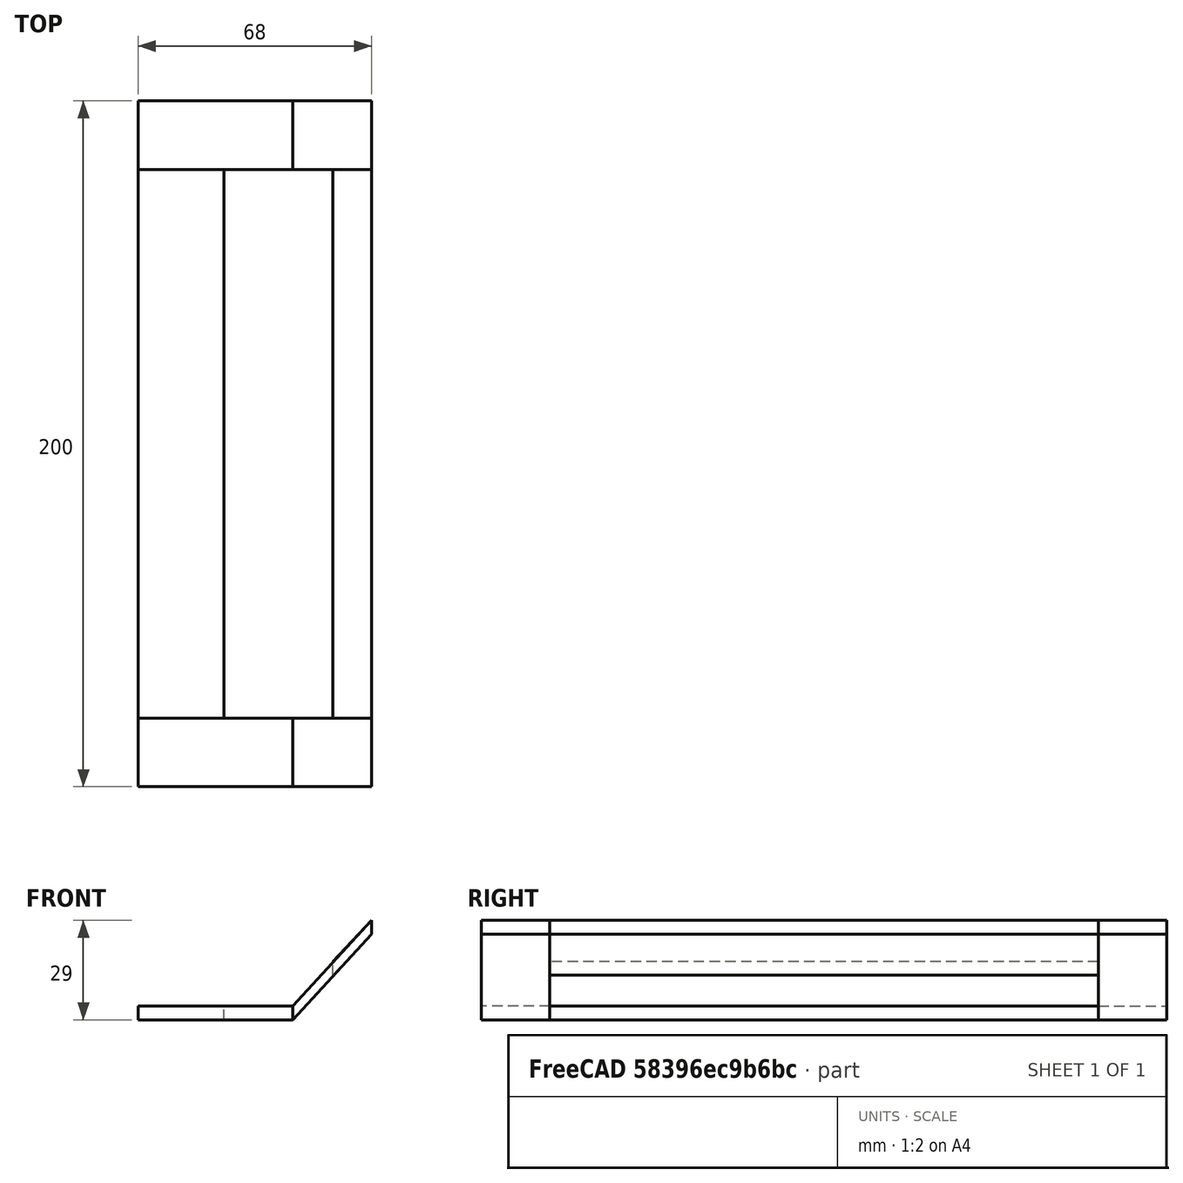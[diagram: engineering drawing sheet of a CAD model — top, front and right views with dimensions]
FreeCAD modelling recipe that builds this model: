
FCSTD DOCUMENT  (FreeCAD 0.15R$WCREV$)
Label: d
License: All rights reserved
LicenseURL: http://en.wikipedia.org/wiki/All_rights_reserved
objects: Part::Part2DObjectPython×8, Part::Feature×8
note: 16 computed .brp shape members not serialized (recipe doc carries the construction recipe); baked Part::Feature solids carry a one-line shape summary decoded from their .brp

FEATURE [Part::Part2DObjectPython] DWire  # Draft 2D object (typed FeaturePython)
  ChamferSize = 0
  Closed = true
  End = (0,20,0)
  FilletRadius = 0
  Length = 130
  MakeFace = true
  Points = (4) [(0,0,0),(45,0,0),(45,20,0),(0,20,0)]
  Start = (0,0,0)
FEATURE [Part::Feature] Shape
  shape: bbox 45 x 20 x 4 mm, 6 faces (baked)
FEATURE [Part::Part2DObjectPython] DWire001  # Draft 2D object (typed FeaturePython)
  ChamferSize = 0
  Closed = true
  End = (25,20,0)
  FilletRadius = 0
  Length = 370
  MakeFace = true
  Points = (4) [(0,20,0),(0,180,0),(25,180,0),(25,20,0)]
  Start = (0,20,0)
FEATURE [Part::Feature] Shape001
  shape: bbox 25 x 160 x 4 mm, 6 faces (baked)
FEATURE [Part::Part2DObjectPython] DWire002  # Draft 2D object (typed FeaturePython)
  ChamferSize = 0
  Closed = true
  End = (45,180,0)
  FilletRadius = 0
  Length = 130
  MakeFace = true
  Points = (4) [(0,180,0),(0,200,0),(45,200,0),(45,180,0)]
  Start = (0,180,0)
FEATURE [Part::Feature] Shape002
  shape: bbox 45 x 20 x 4 mm, 6 faces (baked)
FEATURE [Part::Part2DObjectPython] DWire003  # Draft 2D object (typed FeaturePython)
  ChamferSize = 0
  Closed = true
  End = (25,20,9)
  FilletRadius = 0
  Length = 338
  MakeFace = true
  Points = (4) [(25,20,0),(25,180,0),(25,180,9),(25,20,9)]
  Start = (25,20,0)
FEATURE [Part::Feature] Shape003
  shape: bbox 2e-07 x 160 x 13 mm, 6 faces (baked)
FEATURE [Part::Part2DObjectPython] DWire004  # Draft 2D object (typed FeaturePython)
  ChamferSize = 0
  Closed = true
  End = (45,180,0)
  FilletRadius = 0
  Length = 107.941
  MakeFace = true
  Points = (4) [(45,200,0),(68,200,25),(68,180,25),(45,180,0)]
  Start = (45,200,0)
FEATURE [Part::Feature] Shape004
  shape: bbox 23 x 20 x 29 mm, 6 faces (baked)
FEATURE [Part::Part2DObjectPython] DWire005  # Draft 2D object (typed FeaturePython)
  ChamferSize = 0
  Closed = true
  End = (68,20,25)
  FilletRadius = 0
  Length = 352.966
  MakeFace = true
  Points = (4) [(68,180,25),(56.7,180,13),(56.7,20,13),(68,20,25)]
  Start = (68,180,25)
FEATURE [Part::Feature] Shape005
  shape: bbox 11.3 x 160 x 16 mm, 6 faces (baked)
FEATURE [Part::Part2DObjectPython] DWire006  # Draft 2D object (typed FeaturePython)
  ChamferSize = 0
  Closed = true
  End = (45,20,0)
  FilletRadius = 0
  Length = 107.941
  MakeFace = true
  Points = (4) [(45,0,0),(68,0,25),(68,20,25),(45,20,0)]
  Start = (45,0,0)
FEATURE [Part::Feature] Shape006
  shape: bbox 23 x 20 x 29 mm, 6 faces (baked)
FEATURE [Part::Part2DObjectPython] DWire007  # Draft 2D object (typed FeaturePython)
  ChamferSize = 0
  Closed = true
  End = (68,200,25)
  FilletRadius = 0
  Length = 420
  MakeFace = true
  Points = (5) [(68,200,25),(68,200,35),(68,0,35),(68,0,25),(68,200,25)]
  Start = (68,200,25)
FEATURE [Part::Feature] Shape007
  shape: bbox 2e-07 x 200 x 14 mm, 6 faces (baked)
